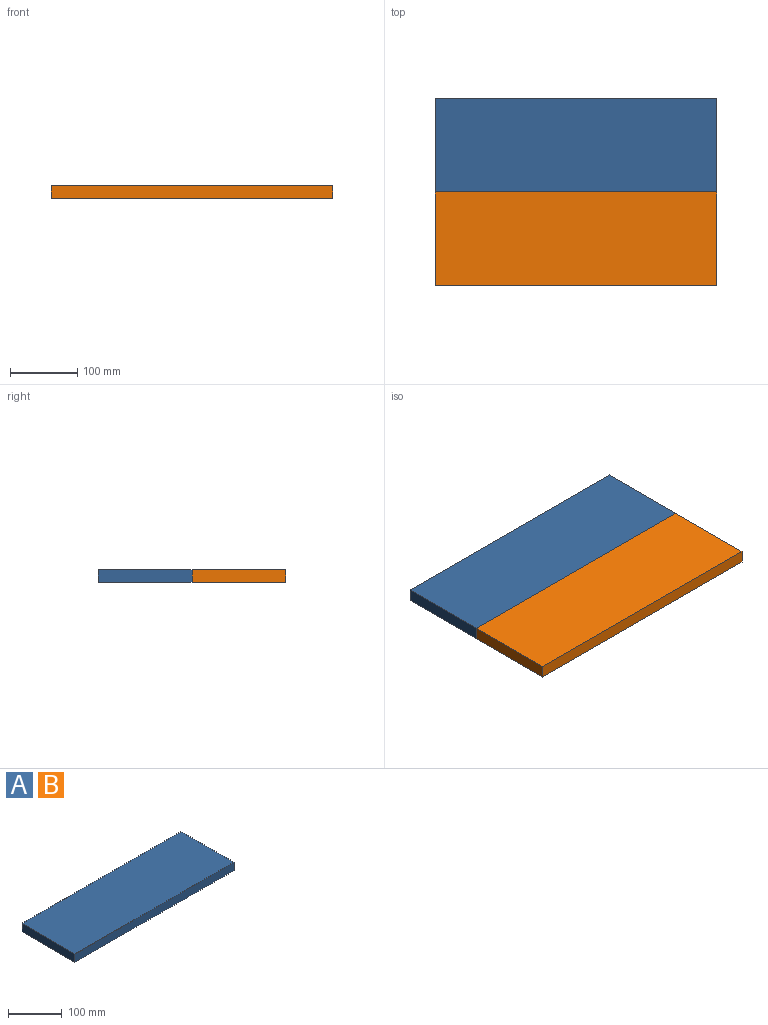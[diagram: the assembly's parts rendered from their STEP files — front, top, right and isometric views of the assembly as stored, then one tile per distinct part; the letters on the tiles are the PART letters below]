
ASSEMBLY  parts=2 mates=1
PART A: 6 faces, bbox 420x140x19 mm
  f0: plane 420x19mm, normal (0,-1,0), area 7980mm2, adj f1,f3,f4,f5
  f1: plane 140x19mm, normal (1,0,0), area 2660mm2, adj f0,f2,f4,f5
  f2: plane 420x19mm, normal (0,1,0), area 7980mm2, adj f1,f3,f4,f5
  f3: plane 140x19mm, normal (-1,0,0), area 2660mm2, adj f0,f2,f4,f5
  f4: plane 420x140mm, normal (0,0,1), area 58800mm2, adj f0,f1,f2,f3
  f5: plane 420x140mm, normal (0,0,-1), area 58800mm2, adj f0,f1,f2,f3
PART B: same geometry as A
PLACE A t=(-167.83,55.21,-59.8)mm
PLACE B t=(-167.83,-84.79,-59.8)mm
MATE fastened A.f0 <-> B.f2  axis (0,-1,0) through (-10.29,30.53,-50.3)mm
